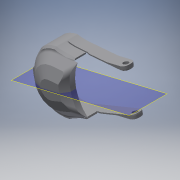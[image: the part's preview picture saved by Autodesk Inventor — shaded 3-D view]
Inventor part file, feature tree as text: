
AUTODESK INVENTOR PART (.ipt)
format: ipt  version: 2016 (Build 200138000, 138)  size: 1,099,264 bytes
history: native  units: in
note: dims shown in document units (in); Inventor stores cm internally (conversion verified against a paired STEP export)
features: extrude x19, sketch x19, fillet x17, projected_geometry x12, chamfer x10, mirror x4, other x3, plane x2, direct_edit x1, move_body x1
ambient origin geometry x8: Origin, YZ Plane, XZ Plane, XY Plane, X Axis, Y Axis, Z Axis, Center Point
bodies: Solid2 (feature_tree), Solid1 (feature_tree)
feature tree (88):
  other  "mount_alt.ipt"
  extrude  "Extrusion1"  Depth=1.0in
  chamfer  "Chamfer1"  Distance=1.0in
  extrude  "Extrusion2"  Depth=0.5in
  extrude  "Extrusion3"  Depth=0.8268in
  extrude  "Extrusion4"  Depth=2.7559in
  plane  "Work Plane1"
  extrude  "Extrusion5"  Depth=0.0625in TaperAngle=0.0deg
  extrude  "Extrusion6"  Depth=0.375in
  fillet  "Fillet1"  Radius=0.125in
  fillet  "Fillet2"  Radius=0.75in
  fillet  "Fillet3"  Radius=0.75in
  extrude  "Extrusion7"  Depth=0.5in TaperAngle=0.0deg
  extrude  "Extrusion9"  Depth=0.25in
  mirror  "Mirror1"
  extrude  "Extrusion8"  Depth=1.0in TaperAngle=0.0deg
  fillet  "Fillet5"  Radius=0.7874in
  chamfer  "Chamfer2"  Distance=0.2756in Angle=45.0deg
  extrude  "Extrusion10"  Depth=1.0in TaperAngle=45.0deg
  chamfer  "Chamfer3"  Distance=1.0in
  extrude  "Extrusion11"  TaperAngle=15.0deg  [1 undecoded]
  direct_edit  "Direct Edit1"
  extrude  "Extrusion12"  Depth=1.0in TaperAngle=0.0deg
  chamfer  "Chamfer4"  Distance=0.125in Angle=45.0deg
  plane  "Work Plane2"
  chamfer  "Chamfer5"  Distance=0.0591in Angle=45.0deg
  chamfer  "Chamfer7"  Distance=0.25in Angle=45.0deg
  fillet  "Fillet11"  Radius=0.25in
  chamfer  "Chamfer8"  Distance=0.0394in Angle=45.0deg
  chamfer  "Chamfer9"  Distance=0.0938in Angle=45.0deg
  fillet  "Fillet14"  Radius=0.5in
  fillet  "Fillet15"  Radius=0.125in
  fillet  "Fillet16"  Radius=0.125in
  extrude  "Extrusion15"  Depth=2.0in
  fillet  "Fillet23"  Radius=1.0in
  fillet  "Fillet24"  Radius=0.125in
  fillet  "Fillet25"  Radius=2.0in
  mirror  "Mirror3"
  extrude  "Extrusion21"  Depth=0.5in
  extrude  "Extrusion16"  Depth=1.0in TaperAngle=45.0deg
  chamfer  "Chamfer10"  Distance=0.5in
  fillet  "Fillet26"  Radius=0.125in
  fillet  "Fillet27"  Radius=0.0787in
  chamfer  "Chamfer11"  Distance=0.25in
  fillet  "Fillet28"  Radius=1.0in
  extrude  "Extrusion17"  Depth=1.0in
  extrude  "Extrusion18"  Depth=1.0in TaperAngle=0.0deg
  extrude  "Extrusion20"  Depth=0.21in
  extrude  "Extrusion19"  Depth=1.0in
  fillet  "Fillet30"  Radius=1.0in
  fillet  "Fillet31"  Radius=1.0in
  fillet  "Fillet34"  Radius=0.1875in
  mirror  "Mirror4"
  mirror  "Mirror5"
  other  "Solid1::mount_alt.ipt"
  other  "TaggingFeature1"
  sketch  "Sketch1"  dims[d0=0.3937in d1=3.3465in d2=1.0in d3=0.0in]
  sketch  "Sketch2"  dims[d4=0.5in d5=0.125in d6=45.0deg d7=1.4173in]
  sketch  "Sketch3"  dims[d8=0.6299in d9=0.0in d10=0.8268in]
  projected_geometry  "Projected Loop1"
  sketch  "Sketch4"  dims[d11=0.315in d12=0.0in d13=2.7559in]
  sketch  "Sketch5"  dims[d14=0.5118in d15=0.0in d16=0.0625in d17=0.0in]
  projected_geometry  "Projected Loop2"
  projected_geometry  "Projected Loop3"
  sketch  "Sketch6"  dims[d18=0.22in d19=0.375in d20=0.125in d21=0.0in d22=0.75in d23=0.75in]
  projected_geometry  "Projected Loop4"
  projected_geometry  "Projected Loop5"
  sketch  "Sketch7"  dims[d24=0.5in d25=0.125in d26=0.0in]
  sketch  "Sketch8"  dims[d27=0.25in d28=0.25in]
  sketch  "Sketch9"  dims[d30=0.125in d31=0.0in d34=1.0in d35=0.0in d37=0.7874in]
  projected_geometry  "Projected Loop6"
  sketch  "Sketch10"  dims[d38=0.0394in]
  projected_geometry  "Projected Loop7"
  sketch  "Sketch11"  dims[d39=0.0197in]
  projected_geometry  "Projected Loop8"
  sketch  "Sketch12"  dims[d40=0.5in d41=0.2756in d42=0.125in d43=45.0deg]
  sketch  "Sketch15"  dims[d44=1.0in d45=0.0in d46=0.125in d47=0.125in d48=45.0deg]
  sketch  "Sketch16"  dims[d49=0.0138in d50=1.0in d51=0.0in]
  projected_geometry  "Projected Loop10"
  sketch  "Sketch17"  dims[d52=0.0in d53=0.0in d54=-0.0079in d55=15.0deg]
  sketch  "Sketch18"  dims[d56=15.0deg d57=1.0in d58=0.0in d59=0.125in d60=0.125in d61=45.0deg d73=0.0591in d74=0.125in d75=45.0deg d82=0.25in d83=0.125in d84=45.0deg d85=0.25in d86=0.0394in d87=0.125in d88=45.0deg d91=0.0938in d92=0.125in d93=45.0deg d94=0.5in d95=0.125in d96=0.125in]
  projected_geometry  "Projected Loop11"
  sketch  "Sketch19"  dims[d98=0.0787in d99=0.75in d100=1.0in d101=0.0in d108=0.125in d109=2.0in]
  sketch  "Sketch20"  dims[d110=0.5in d112=0.0787in]
  sketch  "Sketch21"  dims[d113=1.0in d114=0.0in d115=0.0787in d116=0.125in d117=45.0deg d118=0.5in d119=0.125in d120=0.0787in d121=0.125in d122=45.0deg d123=0.25in d124=1.0in d125=0.0in d126=0.75in d127=1.0in d128=0.0in d130=0.21in d131=0.025in d132=1.0in d133=0.0in d136=1.0in d137=0.0in d138=0.1875in d139=0.0079in d140=0.0in d141=0.75in d146=1.0in d147=0.1562in]
  projected_geometry  "Projected Loop12"
  projected_geometry  "Projected Loop13"
  move_body  "Move1"
note: 1 required parameter value undecoded (feature->parameter linkage not recoverable at this tier; creation-order binding heuristic only, values carry confidence <= 0.55)
